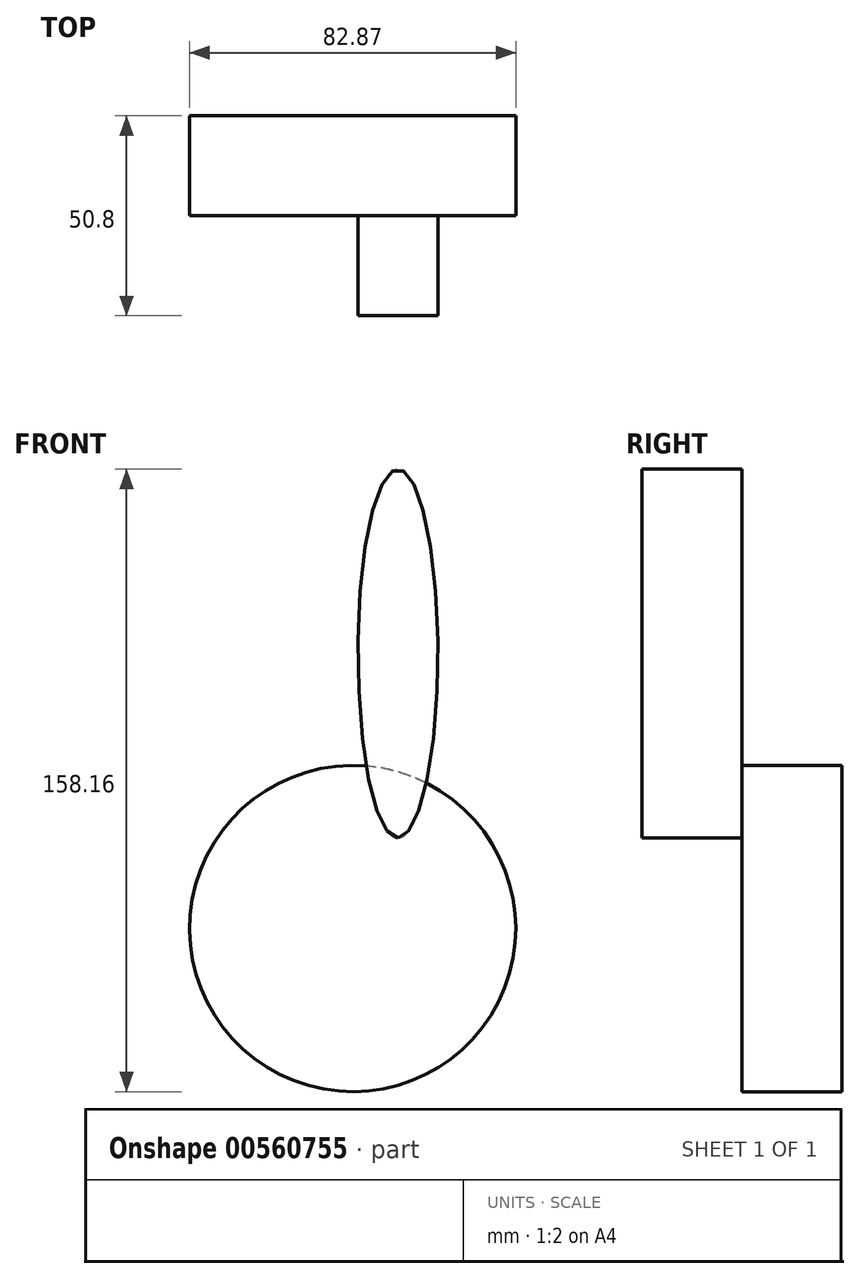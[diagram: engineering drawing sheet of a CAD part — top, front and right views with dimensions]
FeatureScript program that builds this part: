
annotation { "Feature Type Name" : "Feature", "Feature Type Description" : "" }
export const myFeature = defineFeature(function(context is Context, id is Id, definition is map)
    precondition{}
    {
        {
            var Q0;
            Q0=qCreatedBy(makeId("Front.planeOp"),FACE);
            var sketch = newSketch(context, id + "F0", { "sketchPlane" : qUnion([Q0])});
            skCircle(sketch, "E0", {"center": v(55.51, 41.64) * mm, "radius": 41.43 * mm});
            skSolve(sketch);
        }
        {
            var Q0;
            Q0 = qSketchRegion(id + "F0", true);
            extrude(context, id + "F1", {"entities" : qUnion([Q0]), "depth" : 25.4 * mm, "offsetDistance" : 25.4 * mm});
        }
        {
            var Q0;
            Q0=makeQuery(id+"F1.opExtrude","CAP_FACE",FACE,{"disambiguationData":[OSD([sQuery(id+"F0.wireOp",EDGE,"E0")])],"isStart":false});
            var sketch = newSketch(context, id + "F2", { "sketchPlane" : qUnion([Q0])});
            skEllipse(sketch, "E1", {"center": v(67, 111.54) * mm, "majorRadius": 46.83 * mm, "minorRadius": 10.16 * mm, "majorAxis": v(0, -1)});
            skSolve(sketch);
        }
        {
            var Q0;
            Q0 = qSketchRegion(id + "F2", true);
            extrude(context, id + "F3", {"entities" : qUnion([Q0]), "operationType" : NewBodyOperationType.ADD, "depth" : 25.4 * mm, "offsetDistance" : 25.4 * mm});
        }
    });
